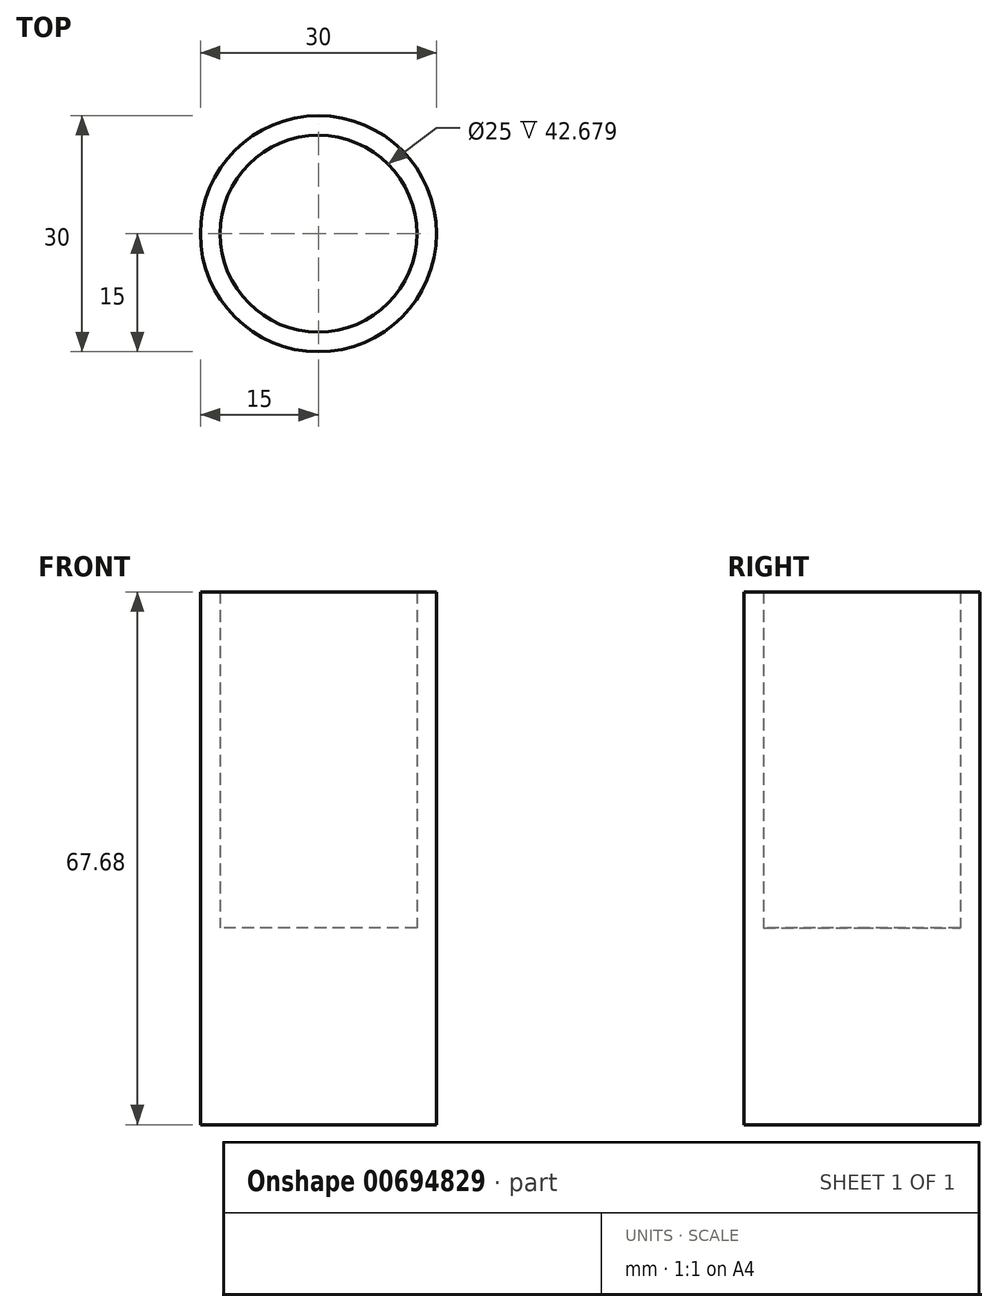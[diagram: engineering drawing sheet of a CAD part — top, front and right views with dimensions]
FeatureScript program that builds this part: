
annotation { "Feature Type Name" : "Feature", "Feature Type Description" : "" }
export const myFeature = defineFeature(function(context is Context, id is Id, definition is map)
    precondition{}
    {
        {
            var Q0;
            Q0=qCreatedBy(makeId("Top.planeOp"),FACE);
            var sketch = newSketch(context, id + "F0", { "sketchPlane" : qUnion([Q0])});
            skCircle(sketch, "E0", {"center": v(0, 0) * mm, "radius": 15 * mm});
            skSolve(sketch);
        }
        {
            var Q0;
            Q0 = qSketchRegion(id + "F0", true);
            var sketch = newSketch(context, id + "F1", { "sketchPlane" : qUnion([Q0])});
            skSolve(sketch);
        }
        {
            var Q0;
            Q0=makeQuery(id+"F1.imprint","IMPRINT",FACE,{"disambiguationData":[TD([[makeQuery(id+"F1.imprint","IMPRINT",EDGE,{"derivedFrom":makeQuery(id+"F0.imprint","IMPRINT",EDGE,{"derivedFrom":sQuery(id+"F0.wireOp",EDGE,"E0")})}),1.0]])]});
            extrude(context, id + "F2", {"entities" : qUnion([Q0]), "depth" : 67.68 * mm, "offsetDistance" : 25 * mm});
        }
        {
            var Q0;
            Q0=makeQuery(id+"F2.opExtrude","CAP_FACE",FACE,{"disambiguationData":[OSD([sQuery(id+"F0.wireOp",EDGE,"E0")])],"isStart":false});
            shell(context, id + "F3", {"entities" : qUnion([Q0]), "thickness" : 2.5 * mm});
        }
        {
            var Q0;
            Q0=makeQuery(id+"F0.imprint","IMPRINT",FACE,{"disambiguationData":[TD([[makeQuery(id+"F0.imprint","IMPRINT",EDGE,{"derivedFrom":sQuery(id+"F0.wireOp",EDGE,"E0")}),1.0]])]});
            extrude(context, id + "F4", {"entities" : qUnion([Q0]), "operationType" : NewBodyOperationType.ADD, "depth" : 25 * mm, "offsetDistance" : 25 * mm});
        }
    });
